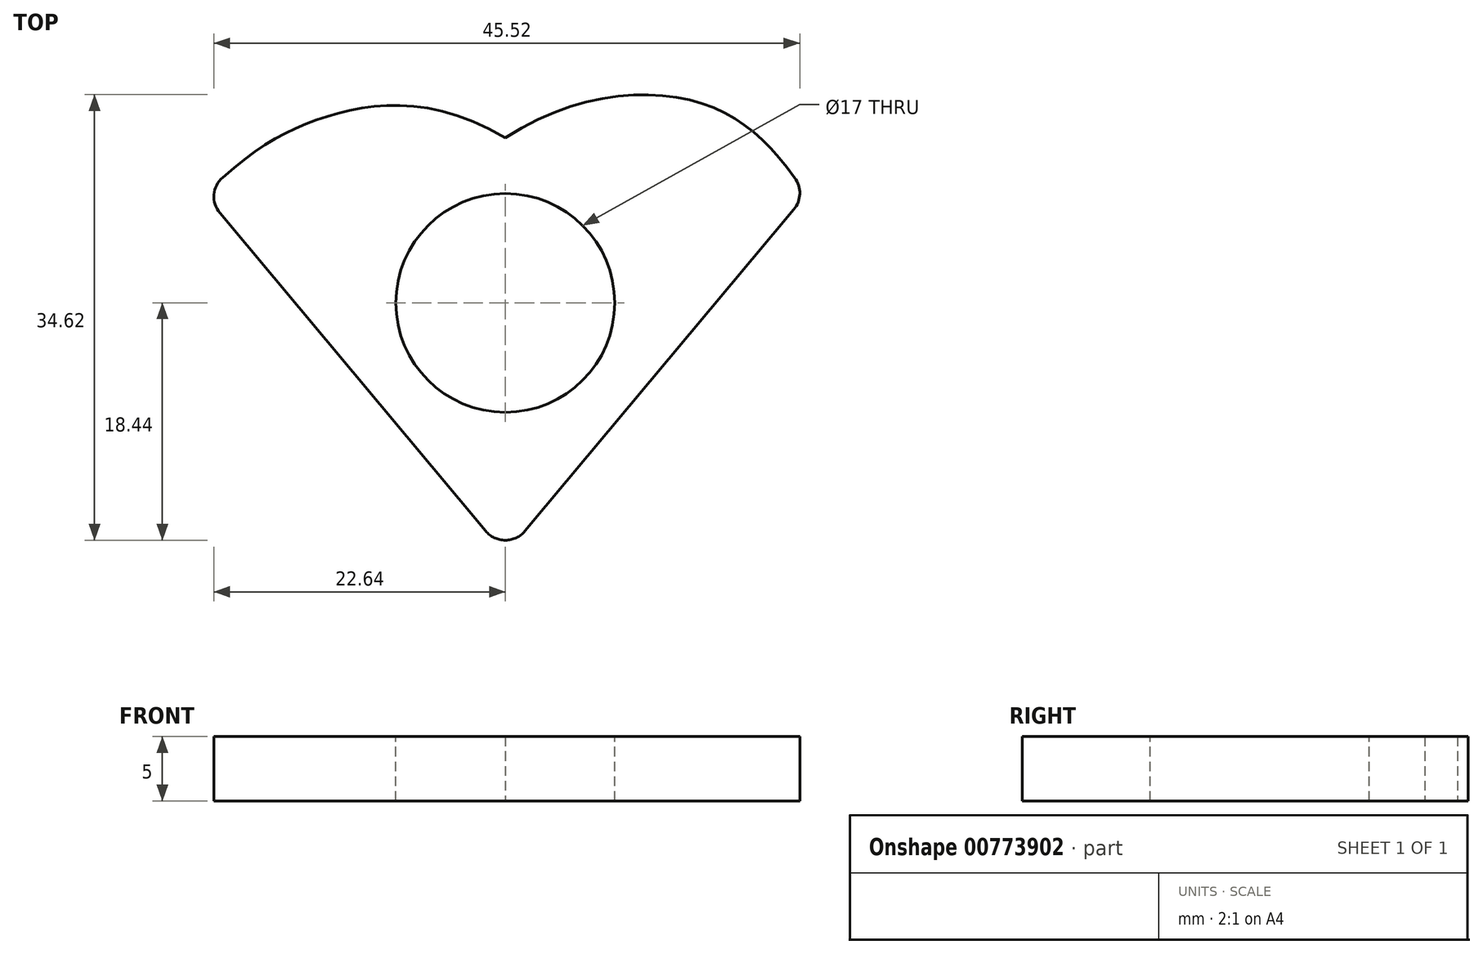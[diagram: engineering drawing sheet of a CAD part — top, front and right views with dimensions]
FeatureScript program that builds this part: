
annotation { "Feature Type Name" : "Feature", "Feature Type Description" : "" }
export const myFeature = defineFeature(function(context is Context, id is Id, definition is map)
    precondition{}
    {
        {
            var Q0;
            Q0=qCreatedBy(makeId("Top.planeOp"),FACE);
            var sketch = newSketch(context, id + "F0", { "sketchPlane" : qUnion([Q0])});
            skLineSegment(sketch, "E0", {"start": v(-23.4, 8.44) * mm, "end": v(0, -19.56) * mm});
            skLineSegment(sketch, "E1", {"start": v(0, -19.56) * mm, "end": v(23.4, 8.44) * mm});
            skFitSpline(sketch, "E2", {"points": [v(23.4, 8.44) * mm, v(15.85, 15.3) * mm, v(0, 12.83) * mm], "startDerivative": vector(-15.05, 21.86) * mm, "endDerivative": vector(-31.05, -20.03) * mm});
            skFitSpline(sketch, "E3", {"points": [v(0, 12.83) * mm, v(-13.76, 14.52) * mm, v(-23.4, 8.44) * mm], "startDerivative": vector(-32.05, 18.75) * mm, "endDerivative": vector(-23.07, -22.03) * mm});
            skSolve(sketch);
        }
        {
            var Q0;
            Q0=makeQuery(id+"F0.imprint","IMPRINT",FACE,{"disambiguationData":[TD([[makeQuery(id+"F0.imprint","IMPRINT",EDGE,{"derivedFrom":sQuery(id+"F0.wireOp",EDGE,"E0")}),1.0]])]});
            extrude(context, id + "F1", {"entities" : qUnion([Q0]), "endBound" : BoundingType.SYMMETRIC, "depth" : 5 * mm, "offsetDistance" : 25.4 * mm});
        }
        {
            var Q0;
            Q0=makeQuery(id+"F1.opExtrude","CAP_FACE",FACE,{"disambiguationData":[OSD([sQuery(id+"F0.wireOp",EDGE,"E0"),sQuery(id+"F0.wireOp",EDGE,"E1"),sQuery(id+"F0.wireOp",EDGE,"E2"),sQuery(id+"F0.wireOp",EDGE,"E3")])],"isStart":false});
            var sketch = newSketch(context, id + "F2", { "sketchPlane" : qUnion([Q0])});
            skCircle(sketch, "E4", {"center": v(0, 0) * mm, "radius": 8.5 * mm});
            skSolve(sketch);
        }
        {
            var Q0;
            Q0=makeQuery(id+"F2.imprint","IMPRINT",FACE,{"disambiguationData":[TD([[makeQuery(id+"F2.imprint","IMPRINT",EDGE,{"derivedFrom":sQuery(id+"F2.wireOp",EDGE,"E4")}),1.0]])]});
            var Q1;
            Q1=sQuery(id+"F2.wireOp",EDGE,"E4");
            extrude(context, id + "F3", {"entities" : qUnion([Q0]), "operationType" : NewBodyOperationType.REMOVE, "surfaceEntities" : qUnion([Q1]), "oppositeDirection" : true, "depth" : 5 * mm, "offsetDistance" : 25.4 * mm});
        }
        {
            var Q0;
            Q0=makeQuery(id+"F1.opExtrude","SWEPT_EDGE",EDGE,{"disambiguationData":[OSD([sQuery(id+"F0.wireOp",EDGE,"E0"),sQuery(id+"F0.wireOp",EDGE,"E3")])]});
            var Q1;
            Q1=makeQuery(id+"F1.opExtrude","SWEPT_EDGE",EDGE,{"disambiguationData":[OSD([sQuery(id+"F0.wireOp",EDGE,"E1"),sQuery(id+"F0.wireOp",EDGE,"E2")])]});
            var Q2;
            Q2=makeQuery(id+"F1.opExtrude","SWEPT_EDGE",EDGE,{"disambiguationData":[OSD([sQuery(id+"F0.wireOp",EDGE,"E0"),sQuery(id+"F0.wireOp",EDGE,"E1")])]});
            fillet(context, id + "F4", {"entities" : qUnion([Q0, Q1, Q2]), "radius" : 2 * mm, "tangentPropagation" : true, "allowEdgeOverflow" : false});
        }
    });
